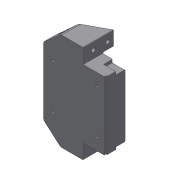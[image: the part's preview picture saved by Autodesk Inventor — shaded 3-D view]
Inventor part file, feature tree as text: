
AUTODESK INVENTOR PART (.ipt)
format: ipt  version: 2018 (Build 220112000, 112)  size: 2,401,280 bytes
history: native  units: mm
features: sketch x51, projected_geometry x44, extrude x43, fillet x19, hole x6, chamfer x5, mirror x3, other x2, plane x2, revolve x1, shell x1, pattern_circular x1, loft x1
ambient origin geometry x8: Origin, YZ Plane, XZ Plane, XY Plane, X Axis, Y Axis, Z Axis, Center Point
bodies: Solid1 (feature_tree), Solid2 (feature_tree), Solid3 (feature_tree)
feature tree (179):
  extrude  "Extrusion1"  Depth=45.0mm
  extrude  "Extrusion2"  Depth=2.25mm
  hole  "Hole1"  [1 undecoded]
  hole  "Hole2"  [1 undecoded]
  fillet  "Fillet1"  Radius=14.0mm
  extrude  "Extrusion3"  Depth=18.5mm
  extrude  "Extrusion4"  Depth=10.0mm
  extrude  "Extrusion5"  Depth=2.0mm
  extrude  "Extrusion6"  Depth=2.0mm
  hole  "Hole3"  [1 undecoded]
  extrude  "Extrusion7"  Depth=2.0mm
  extrude  "Extrusion8"  Depth=5.0mm TaperAngle=0.0deg
  extrude  "Extrusion9"  Depth=10.0mm
  extrude  "Extrusion10"  Depth=10.0mm
  extrude  "Extrusion11"  Depth=14.5mm
  extrude  "Extrusion12"  Depth=14.5mm
  extrude  "Extrusion13"  Depth=5.0mm
  extrude  "Extrusion14"  Depth=2.25mm
  extrude  "Extrusion15"  Depth=5.0mm
  extrude  "Extrusion16"  Depth=9.0mm
  extrude  "Extrusion17"  Depth=1.0mm
  chamfer  "Chamfer1"  Distance=1.0mm
  fillet  "Fillet7"  Radius=20.7mm
  fillet  "Fillet8"  Radius=32.0mm
  mirror  "Mirror1"
  extrude  "Extrusion18"  Depth=1.0mm TaperAngle=0.0deg
  extrude  "Extrusion19"  Depth=8.0mm
  extrude  "Extrusion20"  Depth=0.2mm TaperAngle=0.0deg
  extrude  "Extrusion21"  Depth=0.5mm TaperAngle=0.0deg
  extrude  "Extrusion22"  Depth=3.0mm TaperAngle=0.0deg
  extrude  "Extrusion23"  Depth=0.2mm TaperAngle=0.0deg
  extrude  "Extrusion24"  Depth=2.0mm TaperAngle=45.0deg
  sketch  "Sketch35"  dims[d91=8.0mm d92=0.0mm d93=3.0mm d94=0.0mm]
  other  "Work Axis1"
  revolve  "Revolution1"  [1 undecoded]
  extrude  "Extrusion25"  Depth=4.0mm TaperAngle=0.0deg
  extrude  "Extrusion26"  Depth=19.2mm TaperAngle=0.0deg
  shell  "Shell1"  Thickness=52.1mm
  extrude  "Extrusion27"  Depth=9.0mm
  extrude  "Extrusion28"  Depth=25.0mm
  chamfer  "Chamfer4"  Distance=6.9mm
  chamfer  "Chamfer5"  Distance=2.5mm
  extrude  "Extrusion29"  TaperAngle=90.0deg  [1 undecoded]
  pattern_circular  "Circular Pattern1"  Count=2  [1 undecoded]
  fillet  "Fillet11"  Radius=20.0mm
  fillet  "Fillet12"  Radius=20.0mm
  fillet  "Fillet13"  Radius=6.0mm
  fillet  "Fillet14"  Radius=40.0mm
  chamfer  "Chamfer6"  Distance=40.0mm
  hole  "Hole6"  [1 undecoded]
  extrude  "Extrusion30"  Depth=10.0mm
  fillet  "Fillet15"  Radius=10.0mm
  extrude  "Extrusion31"  Depth=1.0mm TaperAngle=0.0deg
  plane  "Work Plane1"
  loft  "Loft1"
  hole  "Hole8"  [1 undecoded]
  extrude  "Extrusion35"  Depth=1.0mm
  chamfer  "Chamfer7"  Distance=50.0mm
  fillet  "Fillet20"  Radius=50.0mm
  extrude  "Extrusion36"  Depth=2.0mm TaperAngle=45.0deg
  extrude  "Extrusion37"  Depth=1.0mm
  extrude  "Extrusion38"  Depth=1.0mm
  extrude  "Extrusion39"  Depth=1.0mm
  extrude  "Extrusion40"  Depth=1.0mm
  extrude  "Extrusion41"  Depth=1.0mm
  extrude  "Extrusion47"  Depth=1.0mm
  extrude  "Extrusion48"  Depth=1.0mm
  extrude  "Extrusion49"  Depth=1.0mm TaperAngle=0.0deg
  fillet  "Fillet33"  Radius=1.0mm
  extrude  "Extrusion50"  Depth=2.0mm TaperAngle=0.0deg
  hole  "Hole11"  [1 undecoded]
  fillet  "Fillet35"  Radius=150.0mm
  plane  "Work Plane3"
  mirror  "Mirror4"
  fillet  "Fillet34"  [1 undecoded]
  fillet  "Fillet36"  [1 undecoded]
  fillet  "Fillet37"  Radius=45.0mm
  fillet  "Fillet38"  Radius=1.0mm
  fillet  "Fillet39"  Radius=1.0mm
  fillet  "Fillet40"  Radius=30.0mm
  extrude  "Extrusion51"  Depth=1.0mm TaperAngle=0.0deg
  mirror  "Mirror5"
  fillet  "Fillet41"  Radius=118.0mm
  fillet  "Fillet42"  Radius=120.0mm
  sketch  "Sketch1"  dims[d0=24.5mm d1=45.0mm]
  sketch  "Sketch2"  dims[d2=1.95mm d3=0.0mm d4=2.25mm]
  projected_geometry  "Projected Loop1"
  sketch  "Sketch3"  dims[d5=20.0mm d6=2.25mm]
  projected_geometry  "Projected Loop2"
  sketch  "Sketch4"  dims[d7=5.25mm d8=5.25mm d9=14.0mm]
  projected_geometry  "Projected Loop3"
  sketch  "Sketch5"  dims[d10=5.25mm d11=18.5mm]
  projected_geometry  "Projected Loop4"
  sketch  "Sketch6"  dims[d12=10.0mm d13=0.0mm d14=20.5mm]
  projected_geometry  "Projected Loop5"
  sketch  "Sketch7"  dims[d15=2.0mm d16=2.195mm]
  projected_geometry  "Projected Loop6"
  sketch  "Sketch8"  dims[d17=2.0mm]
  projected_geometry  "Projected Loop7"
  sketch  "Sketch9"  dims[d18=2.4mm d19=6.0mm d20=4.4mm d21=2.0mm d22=90.0deg d23=8.0mm d24=20.594885mm d25=20.5mm]
  projected_geometry  "Projected Loop8"
  projected_geometry  "Projected Loop9"
  sketch  "Sketch10"  dims[d26=26.65mm d27=2.0mm]
  projected_geometry  "Projected Loop10"
  projected_geometry  "Projected Loop11"
  sketch  "Sketch11"  dims[d28=2.0mm]
  projected_geometry  "Projected Loop12"
  sketch  "Sketch12"  dims[d29=2.4mm d30=6.0mm d31=4.4mm d32=2.0mm d33=90.0deg d34=8.0mm d35=20.594885mm d36=0.5mm]
  sketch  "Sketch13"  dims[d37=18.0mm d38=5.0mm d39=0.0mm]
  sketch  "Sketch14"  dims[d41=10.0mm d42=0.0mm d43=24.5mm]
  projected_geometry  "Projected Loop13"
  sketch  "Sketch15"  dims[d44=1.15mm d45=0.0mm d46=10.0mm]
  sketch  "Sketch16"  dims[d47=21.0mm d48=14.5mm]
  projected_geometry  "Projected Loop14"
  sketch  "Sketch17"  dims[d49=20.0mm d50=14.5mm]
  projected_geometry  "Projected Loop15"
  sketch  "Sketch18"  dims[d51=24.5mm d52=5.0mm]
  projected_geometry  "Projected Loop16"
  sketch  "Sketch19"  dims[d53=5.0mm d54=2.25mm]
  projected_geometry  "Projected Loop17"
  sketch  "Sketch20"  dims[d55=2.25mm d56=5.0mm]
  projected_geometry  "Projected Loop18"
  sketch  "Sketch22"  dims[d57=5.0mm d58=9.0mm]
  sketch  "Sketch25"  dims[d59=14.75mm d60=4.0mm d61=1.0mm d62=0.0mm d63=20.7mm]
  sketch  "Sketch27"  dims[d64=2.4mm d65=6.0mm d66=4.4mm d67=2.0mm d68=90.0deg d69=8.0mm d70=20.594885mm d72=32.0mm]
  projected_geometry  "Projected Loop22"
  sketch  "Sketch28"  dims[d73=5.0mm d74=0.0mm d75=1.0mm d76=0.0mm]
  projected_geometry  "Projected Loop23"
  sketch  "Sketch29"  dims[d77=12.25mm d78=0.0mm d80=8.0mm]
  projected_geometry  "Projected Loop24"
  sketch  "Sketch30"  dims[d81=4.5mm d82=0.0mm d84=0.2mm d85=0.0mm]
  projected_geometry  "Projected Loop25"
  sketch  "Sketch33"  dims[d86=21.0mm d87=0.5mm d88=0.0mm]
  projected_geometry  "Projected Loop26"
  sketch  "Sketch36"  dims[d95=5.0mm d96=0.0mm d98=0.2mm d99=0.0mm]
  projected_geometry  "Projected Loop27"
  sketch  "Sketch37"  dims[d100=0.2mm d101=0.0mm d102=2.5mm d103=2.0mm d104=45.0deg]
  projected_geometry  "Projected Loop28"
  sketch  "Sketch38"  dims[d105=1.5mm d114=0.5mm]
  projected_geometry  "Projected Loop29"
  projected_geometry  "Projected Loop30"
  projected_geometry  "Projected Loop31"
  projected_geometry  "Projected Loop32"
  sketch  "Sketch39"  dims[d115=22.55mm d116=0.0mm d128=4.0mm d129=0.0mm]
  projected_geometry  "Projected Loop33"
  projected_geometry  "Projected Loop34"
  sketch  "Sketch40"  dims[d130=4.0mm d131=0.0mm d132=19.2mm d133=0.0mm d134=52.1mm]
  projected_geometry  "Projected Loop35"
  sketch  "Sketch41"  dims[d135=6.8mm d136=0.0mm d137=9.0mm]
  projected_geometry  "Projected Loop36"
  sketch  "Sketch42"  dims[d138=9.0mm d139=25.0mm d140=6.9mm d141=0.0mm]
  sketch  "Sketch43"  dims[d142=5.2mm]
  projected_geometry  "Projected Loop37"
  sketch  "Sketch49"  dims[d143=5.2mm]
  other  "Edges1"
  sketch  "Sketch50"  dims[d144=5.2mm]
  sketch  "Sketch51"  dims[d145=5.2mm d146=2.5mm d147=0.0mm]
  sketch  "Sketch52"  dims[d148=5.0mm d149=90.0deg]
  projected_geometry  "Projected Loop40"
  sketch  "Sketch53"  dims[d150=5.0mm]
  sketch  "Sketch55"  dims[d151=105.0mm]
  projected_geometry  "Projected Loop41"
  sketch  "Sketch56"  dims[d152=105.0mm]
  projected_geometry  "Projected Loop42"
  projected_geometry  "Projected Loop43"
  sketch  "Sketch57"  dims[d153=5.0mm d154=0.0mm]
  sketch  "Sketch58"  dims[d156=12.8mm]
  sketch  "Sketch66"  dims[d157=12.8mm]
  sketch  "Sketch67"  dims[d158=12.8mm]
  projected_geometry  "Projected Loop49"
  sketch  "Sketch68"  dims[d159=12.8mm d160=20.0mm d161=20.0mm d162=20.0mm d163=6.0mm d164=40.0mm d165=0.0mm]
  projected_geometry  "Projected Loop50"
  projected_geometry  "Projected Loop51"
  sketch  "Sketch69"  dims[d166=8.0mm d167=40.0mm d168=0.0mm]
  projected_geometry  "Projected Loop52"
  sketch  "Sketch70"  dims[d169=40.0mm d170=0.0mm d178=5.1mm d179=2.45mm d180=45.0deg]
  sketch  "Sketch71"  dims[d181=4.1mm d182=2.45mm d183=45.0deg d184=10.0mm d185=10.0mm d186=40.0mm d187=0.0mm d188=40.0mm d189=360.0deg d191=5.1mm d192=25.0mm d193=50.0mm d194=50.0mm d195=5.0mm d196=2.0mm d197=45.0deg d198=110.0mm d199=77.781746mm d200=77.781746mm d201=4.134mm d202=10.0mm d203=12.6mm d204=2.0mm d205=90.0deg d206=14.2mm d207=20.594885mm d208=11.0mm d209=11.0mm d210=11.0mm d211=11.0mm d212=45.0mm d213=0.0mm d214=1.0mm d215=2.0mm d216=0.0mm d236=45.0mm d237=150.0mm d238=0.0mm d239=90.0deg d240=0.0mm d241=90.0deg d242=4.134mm d243=10.0mm d244=4.0mm d245=2.0mm d246=90.0deg d247=14.2mm d248=20.594885mm d249=45.0mm d250=0.0mm d251=1.0mm d252=2.0mm d253=45.0deg d254=1.0mm d255=30.0mm d256=0.0mm d257=25.0mm d258=0.0mm d270=118.0mm d271=120.0mm d272=21.109127mm d273=21.109127mm d274=4.0mm d275=0.0mm d276=16.0mm d277=0.5mm d278=30.0mm d279=0.0mm d280=30.0mm d281=0.0mm d284=30.0mm d285=0.0mm d323=48.0mm d324=40.0mm d325=172.0mm d326=26.0mm d327=26.0mm d328=8.5mm d329=0.0mm d330=0.0mm d331=20.0mm d332=0.0mm d334=3.0mm d335=18.0mm d336=20.0mm d337=0.0mm d338=2.0mm d339=2.0mm d340=3.175mm d341=0.0mm d342=1.0mm d343=25.4mm d344=18.0mm d345=12.7mm d346=6.756mm d347=6.0mm d348=11.113mm d349=64.0mm d350=14.3117mm d351=8.0mm d352=20.594885mm d353=1.0mm d354=1.25mm d355=5.0mm d356=2.0mm d357=1.0mm d358=1.0mm d359=22.0mm d360=16.0mm d361=5.0mm d362=0.0mm d363=1.0mm d364=1.0mm]
  projected_geometry  "Projected Loop53"
  projected_geometry  "Project Cut Edges1"
note: 11 required parameter values undecoded (feature->parameter linkage not recoverable at this tier; creation-order binding heuristic only, values carry confidence <= 0.55)